# Revit family: DIVITYP003
name_source: partatom
category: Furniture
units: mm (PartAtom-declared; Revit-internal decimal feet)

## family parameters
Always vertical = Yes
Cut with Voids When Loaded = No
OmniClass Number = 23.40.20.00
OmniClass Title = General Furniture and Specialties
Render Appearance Source = Family Geometry
Room Calculation Point = No
Shared = No
Work Plane-Based = No

## types (1)
- DIVITYP003
    Cost = 66471 $
    Default Elevation = 0 mm  [stored 0 ft]
    Description = 3 x White Duplex Outlet - Line 1, 3 x White Duplex Outlet - Line 2, 3 x White Duplex Outlet - Line 3, 3 x White Duplex Outlet - Line 4 - Dedicated, 2 x 57 in. Electrical Jumper  (Pt 36E & Vt 48), 1 x 18 in. Electrical Jumper  (Panel To Panel), 1 x LH Receptacle Mounted Base Infeed - 72L - 8 Wire, 4 Circuit, 2 x DiVi LINEAR BASE RACEWAY SHROUD 3-WAY 90 DEGREES, 6 x DiVi LINEAR BASE RACEWAY SHROUD 2-WAY 90 DEGREES, 4 x DiVi LINEAR HARD PANEL-PWR-PERM MONO- 42H X 36W, 24 x DiVi LINEAR HARD PANEL -NPWR-PERMANENT MONOLITHIC- 42H X 36W, 8 x DIVI LINEAR BASE RACEWAY SHROUD END OF RUN, 6 x Pedestal - Box,Box,File - 30D, 6 x Pedestal - F/F - 24D, 6 x Silver Key Alike Kit (2 Cores) - Wesko Type, 6 x Rectangular - 2mm Edge - 24D x 42W, 6 x Bullpen Worksurface - Rect 30"D x 72 1/4"W, 18 x Flat Plate, 3 x Regular Cantilever - Left Hand - 30D, 3 x Regular Cantilever - Right Hand - 30D, 6 x U-Channel - 48W, 6 x Divi Channel Screen, Panel Top,GL1/4",12hx36w, 11 x Divi Channel Screen, Panel Top,GL1/4",12hx72w
    Exported From CET Designer = Yes
    Manufacturer = AIS
    Model = E-MW8W4DO1-W
    Show DIVITYP003 = Yes
    VisibilityIndex = 0

note: [stored X ft] marks values corroborated as IEEE doubles in the binary element streams (Revit-internal decimal feet)

## geometry (parser evidence)
native form markers: Sweep x2
no freeform markers — native parametric forms only
